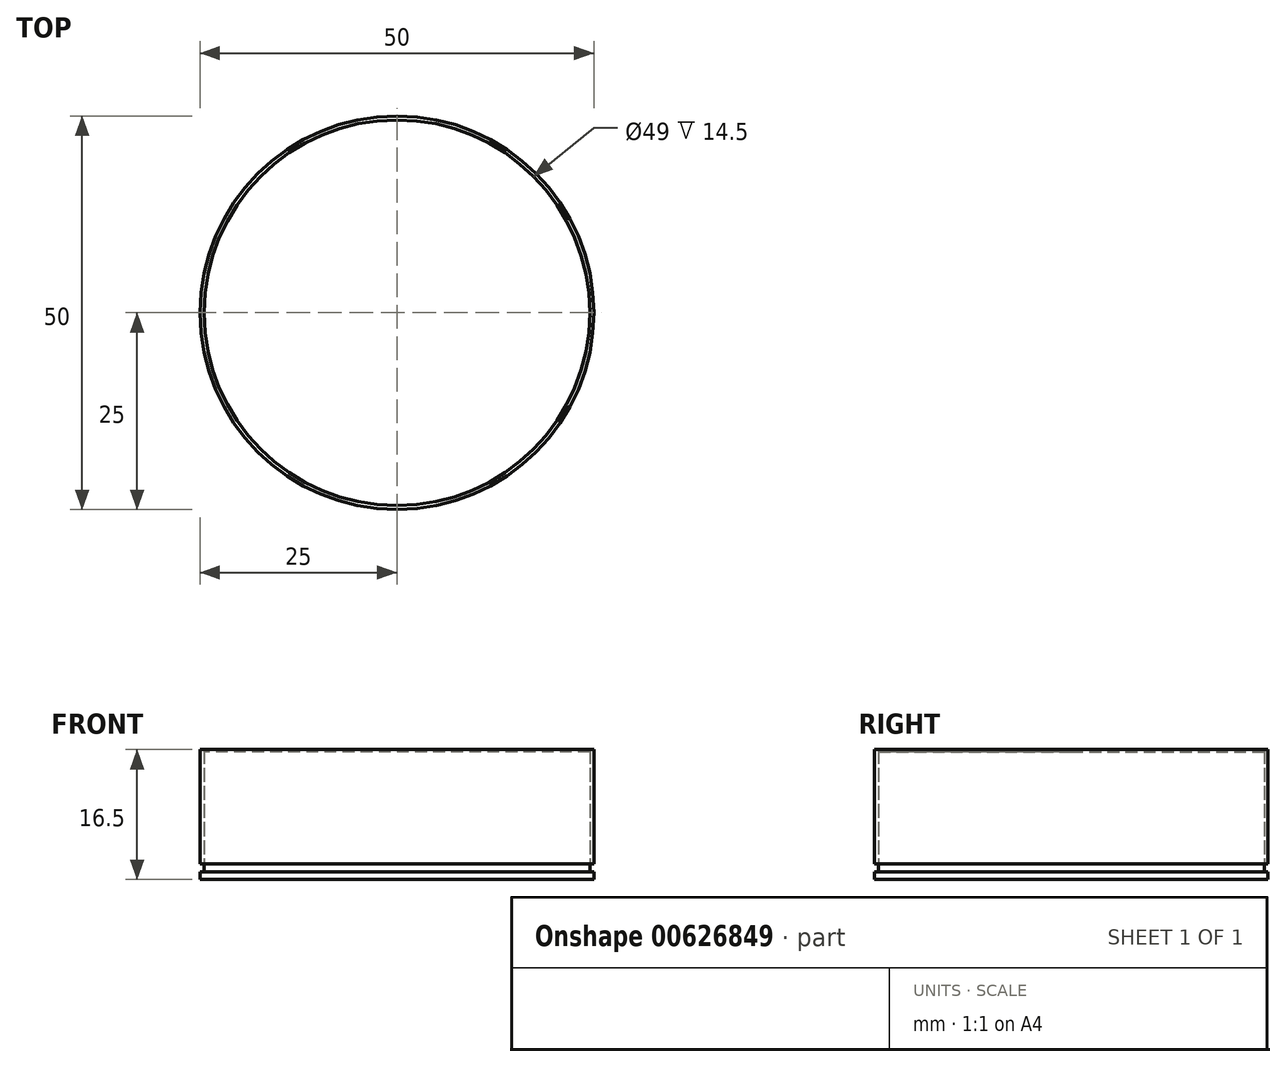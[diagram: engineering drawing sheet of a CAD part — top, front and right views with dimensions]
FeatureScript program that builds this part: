
annotation { "Feature Type Name" : "Feature", "Feature Type Description" : "" }
export const myFeature = defineFeature(function(context is Context, id is Id, definition is map)
    precondition{}
    {
        {
            var Q0;
            Q0=qCreatedBy(makeId("Top.planeOp"),FACE);
            var sketch = newSketch(context, id + "F0", { "sketchPlane" : qUnion([Q0])});
            skCircle(sketch, "E0", {"center": v(0, 0) * mm, "radius": 25 * mm});
            skSolve(sketch);
        }
        {
            var Q0;
            Q0=makeQuery(id+"F0.imprint","IMPRINT",FACE,{"disambiguationData":[TD([[makeQuery(id+"F0.imprint","IMPRINT",EDGE,{"derivedFrom":sQuery(id+"F0.wireOp",EDGE,"E0")}),1.0]])]});
            extrude(context, id + "F1", {"entities" : qUnion([Q0]), "depth" : 1 * mm, "offsetDistance" : 25 * mm});
        }
        {
            var Q0;
            Q0=makeQuery(id+"F1.opExtrude","CAP_FACE",FACE,{"disambiguationData":[OSD([sQuery(id+"F0.wireOp",EDGE,"E0")])],"isStart":false});
            var sketch = newSketch(context, id + "F2", { "sketchPlane" : qUnion([Q0])});
            skCircle(sketch, "E1", {"center": v(0, 0) * mm, "radius": 24.5 * mm});
            skSolve(sketch);
        }
        {
            var Q0;
            Q0=makeQuery(id+"F2.imprint","IMPRINT",FACE,{"disambiguationData":[TD([[makeQuery(id+"F2.imprint","IMPRINT",EDGE,{"derivedFrom":sQuery(id+"F2.wireOp",EDGE,"E1")}),1.0]])]});
            extrude(context, id + "F3", {"entities" : qUnion([Q0]), "operationType" : NewBodyOperationType.ADD, "depth" : 1 * mm, "offsetDistance" : 25 * mm});
        }
        {
            var Q0;
            Q0=makeQuery(id+"F3.opExtrude","CAP_FACE",FACE,{"disambiguationData":[OSD([sQuery(id+"F2.wireOp",EDGE,"E1")])],"isStart":false});
            var sketch = newSketch(context, id + "F4", { "sketchPlane" : qUnion([Q0])});
            skCircle(sketch, "E2", {"center": v(0, 0) * mm, "radius": 25 * mm});
            skSolve(sketch);
        }
        {
            var Q0;
            Q0=makeQuery(id+"F4.imprint","IMPRINT",FACE,{"disambiguationData":[TD([[makeQuery(id+"F4.imprint","IMPRINT",EDGE,{"derivedFrom":makeQuery(id+"F3.opExtrude","CAP_EDGE",EDGE,{"disambiguationData":[OSD([sQuery(id+"F2.wireOp",EDGE,"E1")])],"isStart":false})}),1.0]])]});
            var sketch = newSketch(context, id + "F5", { "sketchPlane" : qUnion([Q0])});
            skCircle(sketch, "E3", {"center": v(0, 0) * mm, "radius": 25 * mm});
            skSolve(sketch);
        }
        {
            var Q0;
            Q0=makeQuery(id+"F4.imprint","IMPRINT",FACE,{"disambiguationData":[TD([[makeQuery(id+"F4.imprint","IMPRINT",EDGE,{"derivedFrom":sQuery(id+"F4.wireOp",EDGE,"E2")}),1.0]])]});
            extrude(context, id + "F6", {"entities" : qUnion([Q0]), "depth" : 14.5 * mm, "offsetDistance" : 25 * mm});
        }
        {
            var Q0;
            Q0=makeQuery(id+"F5.imprint","IMPRINT",FACE,{"disambiguationData":[TD([[makeQuery(id+"F5.imprint","IMPRINT",EDGE,{"derivedFrom":makeQuery(id+"F4.imprint","IMPRINT",EDGE,{"derivedFrom":makeQuery(id+"F3.opExtrude","CAP_EDGE",EDGE,{"disambiguationData":[OSD([sQuery(id+"F2.wireOp",EDGE,"E1")])],"isStart":false})})}),1.0]])]});
            extrude(context, id + "F7", {"entities" : qUnion([Q0]), "depth" : 14.2 * mm, "offsetDistance" : 25 * mm});
        }
    });
